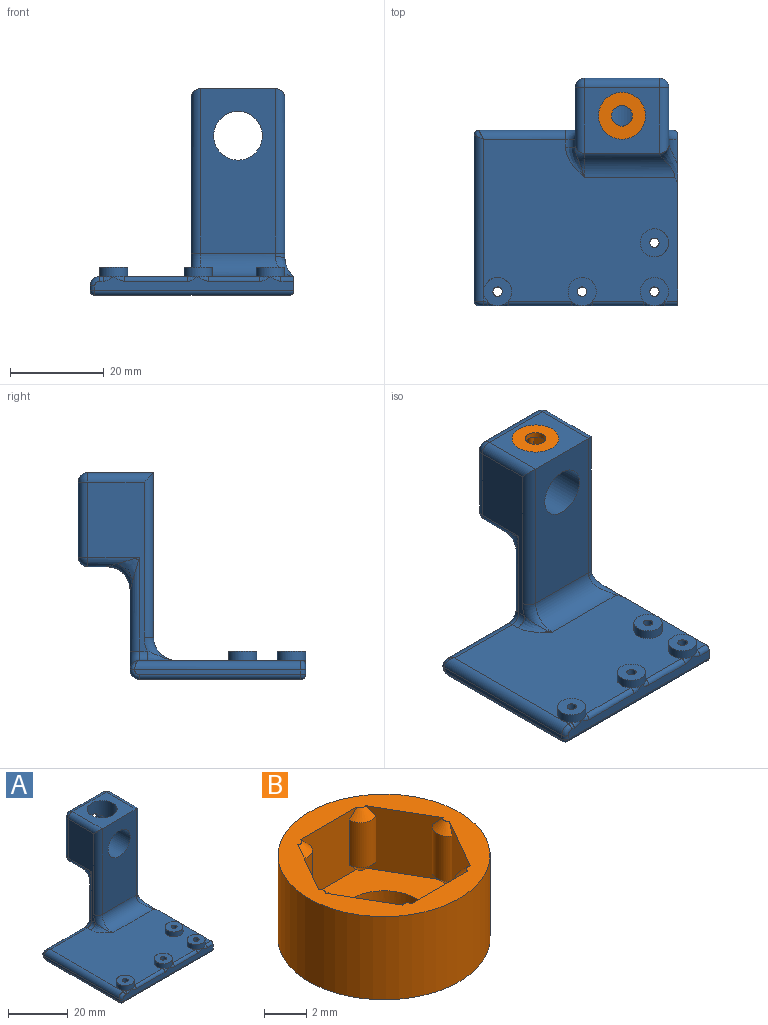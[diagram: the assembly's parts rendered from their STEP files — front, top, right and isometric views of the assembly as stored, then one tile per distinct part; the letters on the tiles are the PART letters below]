
ASSEMBLY  parts=2 mates=1
PART A: 79 faces, bbox 46x50.4x46.2 mm
  f0: cylinder r=5mm len=14.53mm, axis (1,0,0), area 114.1mm2, adj f1,f11,f12,f58
  f1: bspline ~5.64x5.64mm, area 16.6mm2, adj f0,f2,f11,f12,f44,f48
  f2: bspline ~5.37x5.37mm, area 6.6mm2, adj f1,f44,f48
  f3: bspline ~5.37x5.37mm, area 6.6mm2, adj f38,f40,f58
  f4: plane 43.4x36.4mm, normal (0,0,1), area 1136.7mm2, adj f14,f24,f26,f28,f30,f31,f33,f34
  f5: cylinder r=5.2mm len=16mm, axis (0,-1,0), area 427.7mm2, adj f6,f7,f13
  f6: plane 35x16mm, normal (0,-1,0), area 475.1mm2, adj f5,f9,f31,f42,f55
  f7: plane 16x16mm, normal (0,1,0), area 171.1mm2, adj f5,f46,f47,f51,f52
  f8: plane 34.08x12.08mm, normal (1,0,0), area 210.1mm2, adj f32,f44,f48,f52,f54,f55,f56
  f9: plane 16x14mm, normal (0,0,1), area 145.5mm2, adj f6,f13,f45,f51,f54
  f10: plane 36x12.68mm, normal (-1,0,0), area 212.7mm2, adj f34,f38,f39,f40,f42,f45,f46
  f11: plane 22.96x17.06mm, normal (0,1,0), area 281.1mm2, adj f0,f1,f35,f36,f38,f41,f44,f58
  f12: plane 16.06x4.06mm, normal (0,0,-1), area 64mm2, adj f0,f1,f40,f47,f48,f58
  f13: cylinder r=5mm len=10mm, axis (0,0,1), area 201.4mm2, adj f5,f9
  f14: plane 37.36x3.96mm, normal (1,0,0), area 108.4mm2, adj f4,f15,f32,f41,f57,f59,f60,f62
  f15: plane 42.4x3mm, normal (0,-1,0), area 89.5mm2, adj f14,f64,f65,f67,f69,f70,f71,f72
  f16: plane 35.4x1mm, normal (-1,0,0), area 35.2mm2, adj f33,f63,f66,f70
  f17: plane 41.4x34.4mm, normal (0,0,-1), area 1411.6mm2, adj f19,f20,f21,f22,f36,f62,f65,f66
  f18: plane 2x0.76mm, normal (0,0,1), area 0.5mm2, adj f24,f33,f67
  f19: cylinder r=1mm len=6mm, axis (0,0,-1), area 37.7mm2, adj f17,f27
  f20: cylinder r=1mm len=6mm, axis (0,0,-1), area 37.7mm2, adj f17,f25
  f21: cylinder r=1mm len=6mm, axis (0,0,-1), area 37.7mm2, adj f17,f29
  f22: cylinder r=1mm len=6mm, axis (0,0,-1), area 37.7mm2, adj f17,f23
  f23: plane 6x6mm, normal (0,0,1), area 25.1mm2, adj f22,f24
  f24: cylinder r=3mm len=6mm, axis (0,0,-1), area 37.7mm2, adj f4,f18,f23,f64,f78
  f25: plane 6x6mm, normal (0,0,1), area 25.1mm2, adj f20,f26
  f26: cylinder r=3mm len=6mm, axis (0,0,-1), area 37.7mm2, adj f4,f25,f75,f76
  f27: plane 6x6mm, normal (0,0,1), area 25.1mm2, adj f19,f28
  f28: cylinder r=3mm len=6mm, axis (0,0,-1), area 37.7mm2, adj f4,f27,f72,f73
  f29: plane 6x6mm, normal (0,0,1), area 25.1mm2, adj f21,f30
  f30: cylinder r=3mm len=6mm, axis (0,0,-1), area 37.7mm2, adj f4,f29
  f31: cylinder r=5mm len=19.27mm, axis (1,0,0), area 136.5mm2, adj f4,f6,f39,f56,f57
  f32: cylinder r=5mm len=5.58mm, axis (0,1,0), area 12mm2, adj f8,f14,f41,f57
  f33: cylinder r=2mm len=35.4mm, axis (0,1,0), area 109.6mm2, adj f4,f16,f18,f61,f69
  f34: cylinder r=2mm len=2mm, axis (0,-1,0), area 5.3mm2, adj f4,f10,f35,f37
  f35: torus R=4mm, axis (0,-1,0), area 13.5mm2, adj f11,f34,f36,f38
  f36: cylinder r=2mm len=41.4mm, axis (1,0,0), area 186.6mm2, adj f4,f11,f17,f35,f60,f61,f63
  f37: bspline ~7.51x4mm, area 7.3mm2, adj f4,f34,f39
  f38: cylinder r=2mm len=20mm, axis (0,0,-1), area 49.6mm2, adj f3,f10,f11,f35,f58
  f39: torus R=7mm, axis (1,0,0), area 17.5mm2, adj f10,f31,f37,f42
  f40: cylinder r=2mm len=11mm, axis (0,1,0), area 21.3mm2, adj f3,f10,f12,f43,f58
  f41: torus R=7mm, axis (0,-1,0), area 17mm2, adj f11,f14,f32,f44,f59
  f42: cylinder r=2mm len=35mm, axis (0,0,-1), area 106.8mm2, adj f6,f10,f39,f45
  f43: sphere r=2mm, area 8.6mm2, adj f40,f46,f47
  f44: cylinder r=2mm len=18.08mm, axis (0,0,1), area 43.6mm2, adj f1,f2,f8,f11,f41
  f45: cylinder r=2mm len=14mm, axis (0,1,0), area 40.8mm2, adj f9,f10,f42,f49
  f46: cylinder r=2mm len=16mm, axis (0,0,1), area 50.3mm2, adj f7,f10,f43,f49
  f47: cylinder r=2mm len=16mm, axis (1,0,0), area 50.3mm2, adj f7,f12,f43,f50
  f48: cylinder r=2mm len=11mm, axis (0,-1,0), area 21.3mm2, adj f1,f2,f8,f12,f50
  f49: sphere r=2mm, area 8.6mm2, adj f45,f46,f51
  f50: sphere r=2mm, area 4mm2, adj f47,f48,f52
  f51: cylinder r=2mm len=16mm, axis (1,0,0), area 50.3mm2, adj f7,f9,f49,f53
  f52: cylinder r=2mm len=16mm, axis (0,0,-1), area 50.3mm2, adj f7,f8,f50,f53
  f53: sphere r=2mm, area 4mm2, adj f51,f52,f54
  f54: cylinder r=2mm len=14mm, axis (0,-1,0), area 40.8mm2, adj f8,f9,f53,f55
  f55: cylinder r=2mm len=35mm, axis (0,0,1), area 106.8mm2, adj f6,f8,f54,f56
  f56: torus R=7mm, axis (1,0,0), area 2.8mm2, adj f8,f31,f55,f57
  f57: bspline ~9.99x5.39mm, area 18.3mm2, adj f4,f14,f31,f32,f56
  f58: bspline ~5.64x5.64mm, area 16.6mm2, adj f0,f3,f11,f12,f38,f40
  f59: cylinder r=1mm len=1.66mm, axis (0,0,1), area 1.5mm2, adj f11,f14,f41,f60
  f60: torus R=1mm, axis (-1,0,0), area 4mm2, adj f14,f36,f59,f62
  f61: bspline ~2.1x2mm, area 2.2mm2, adj f33,f36,f63
  f62: cylinder r=1mm len=35.4mm, axis (0,1,0), area 54.8mm2, adj f14,f17,f60,f65
  f63: torus R=1mm, axis (-1,0,0), area 4mm2, adj f16,f36,f61,f66
  f64: bspline ~2.24x1mm, area 1.1mm2, adj f15,f24,f67
  f65: cylinder r=1mm len=42.4mm, axis (1,0,0), area 65.8mm2, adj f15,f17,f62,f68
  f66: cylinder r=1mm len=34.4mm, axis (0,-1,0), area 54mm2, adj f16,f17,f63,f68
  f67: cylinder r=1mm len=1mm, axis (-1,0,0), area 1.2mm2, adj f15,f18,f64,f69
  f68: sphere r=1mm, area 1.6mm2, adj f65,f66,f70
  f69: torus R=1mm, axis (0,-1,0), area 4mm2, adj f15,f33,f67,f70
  f70: cylinder r=1mm len=1mm, axis (0,0,1), area 1.6mm2, adj f15,f16,f68,f69
  f71: cylinder r=1mm len=2.76mm, axis (-1,0,0), area 4.3mm2, adj f4,f14,f15,f72
  f72: bspline ~2.24x1mm, area 1.1mm2, adj f15,f28,f71
  f73: bspline ~2.24x1mm, area 1.1mm2, adj f15,f28,f74
  f74: cylinder r=1mm len=10.93mm, axis (-1,0,0), area 17.2mm2, adj f4,f15,f73,f75
  f75: bspline ~2.24x1mm, area 1.1mm2, adj f15,f26,f74
  f76: bspline ~2.24x1mm, area 1.1mm2, adj f15,f26,f77
  f77: cylinder r=1mm len=13.53mm, axis (-1,0,0), area 21.2mm2, adj f4,f15,f76,f78
  f78: bspline ~2.24x1mm, area 1.1mm2, adj f15,f24,f77
PART B: 29 faces, bbox 10x10x4.8 mm
  f0: plane 3.77x3.6mm, normal (0,-1,0), area 10.5mm2, adj f7,f8,f9,f10,f17,f18,f19,f26
  f1: plane 3.6x3.27mm, normal (-0.87,-0.5,0), area 10.5mm2, adj f7,f8,f9,f10,f14,f15,f16,f26
  f2: plane 3.6x3.27mm, normal (-0.87,0.5,0), area 10.5mm2, adj f7,f11,f12,f13,f14,f15,f16,f26
  f3: plane 3.77x3.6mm, normal (0,1,0), area 10.5mm2, adj f7,f11,f12,f13,f23,f24,f25,f26
  f4: plane 3.6x3.27mm, normal (0.87,0.5,0), area 10.5mm2, adj f7,f20,f21,f22,f23,f24,f25,f26
  f5: cylinder r=5mm len=10mm, axis (0,0,-1), area 150.8mm2, adj f7,f27
  f6: plane 3.6x3.27mm, normal (0.87,-0.5,0), area 10.5mm2, adj f7,f17,f18,f19,f20,f21,f22,f26
  f7: plane 10x10mm, normal (0,0,1), area 31.5mm2, adj f0,f1,f2,f3,f4,f5,f6,f9
  f8: cylinder r=0.75mm len=2.6mm, axis (0,0,-1), area 4.1mm2, adj f0,f1,f9,f10
  f9: cone r=0.25mm half-angle=45deg, axis (0,0,-1), area 0.7mm2, adj f0,f1,f7,f8
  f10: cone r=0.75mm half-angle=45deg, axis (0,0,1), area 0.7mm2, adj f0,f1,f8,f26
  f11: cylinder r=0.75mm len=2.6mm, axis (0,0,-1), area 4.1mm2, adj f2,f3,f12,f13
  f12: cone r=0.25mm half-angle=45deg, axis (0,0,-1), area 0.7mm2, adj f2,f3,f7,f11
  f13: cone r=0.75mm half-angle=45deg, axis (0,0,1), area 0.7mm2, adj f2,f3,f11,f26
  f14: cylinder r=0.75mm len=2.6mm, axis (0,0,-1), area 4.1mm2, adj f1,f2,f15,f16
  f15: cone r=0.25mm half-angle=45deg, axis (0,0,-1), area 0.7mm2, adj f1,f2,f7,f14
  f16: cone r=0.75mm half-angle=45deg, axis (0,0,1), area 0.7mm2, adj f1,f2,f14,f26
  f17: cone r=0.75mm half-angle=45deg, axis (0,0,1), area 0.7mm2, adj f0,f6,f19,f26
  f18: cone r=0.25mm half-angle=45deg, axis (0,0,-1), area 0.7mm2, adj f0,f6,f7,f19
  f19: cylinder r=0.75mm len=2.6mm, axis (0,0,-1), area 4.1mm2, adj f0,f6,f17,f18
  f20: cone r=0.75mm half-angle=45deg, axis (0,0,1), area 0.7mm2, adj f4,f6,f22,f26
  f21: cone r=0.25mm half-angle=45deg, axis (0,0,-1), area 0.7mm2, adj f4,f6,f7,f22
  f22: cylinder r=0.75mm len=2.6mm, axis (0,0,-1), area 4.1mm2, adj f4,f6,f20,f21
  f23: cylinder r=0.75mm len=2.6mm, axis (0,0,-1), area 4.1mm2, adj f3,f4,f24,f25
  f24: cone r=0.25mm half-angle=45deg, axis (0,0,-1), area 0.7mm2, adj f3,f4,f7,f23
  f25: cone r=0.75mm half-angle=45deg, axis (0,0,1), area 0.7mm2, adj f3,f4,f23,f26
  f26: plane 8.29x7.4mm, normal (0,0,1), area 31.8mm2, adj f0,f1,f2,f3,f4,f6,f10,f13
  f27: plane 10x10mm, normal (0,0,-1), area 63.3mm2, adj f5,f28
  f28: cylinder r=2.2mm len=4.4mm, axis (0,0,-1), area 16.6mm2, adj f26,f27
PLACE A t=(-4.08,3.25,-6.33)mm
PLACE B rot(axis=(1,0,0),180deg) t=(-4.08,6.25,22.09)mm
MATE fastened B.f5 <-> A.f13  axis (0,0,1) through (-4.08,6.25,23.29)mm
